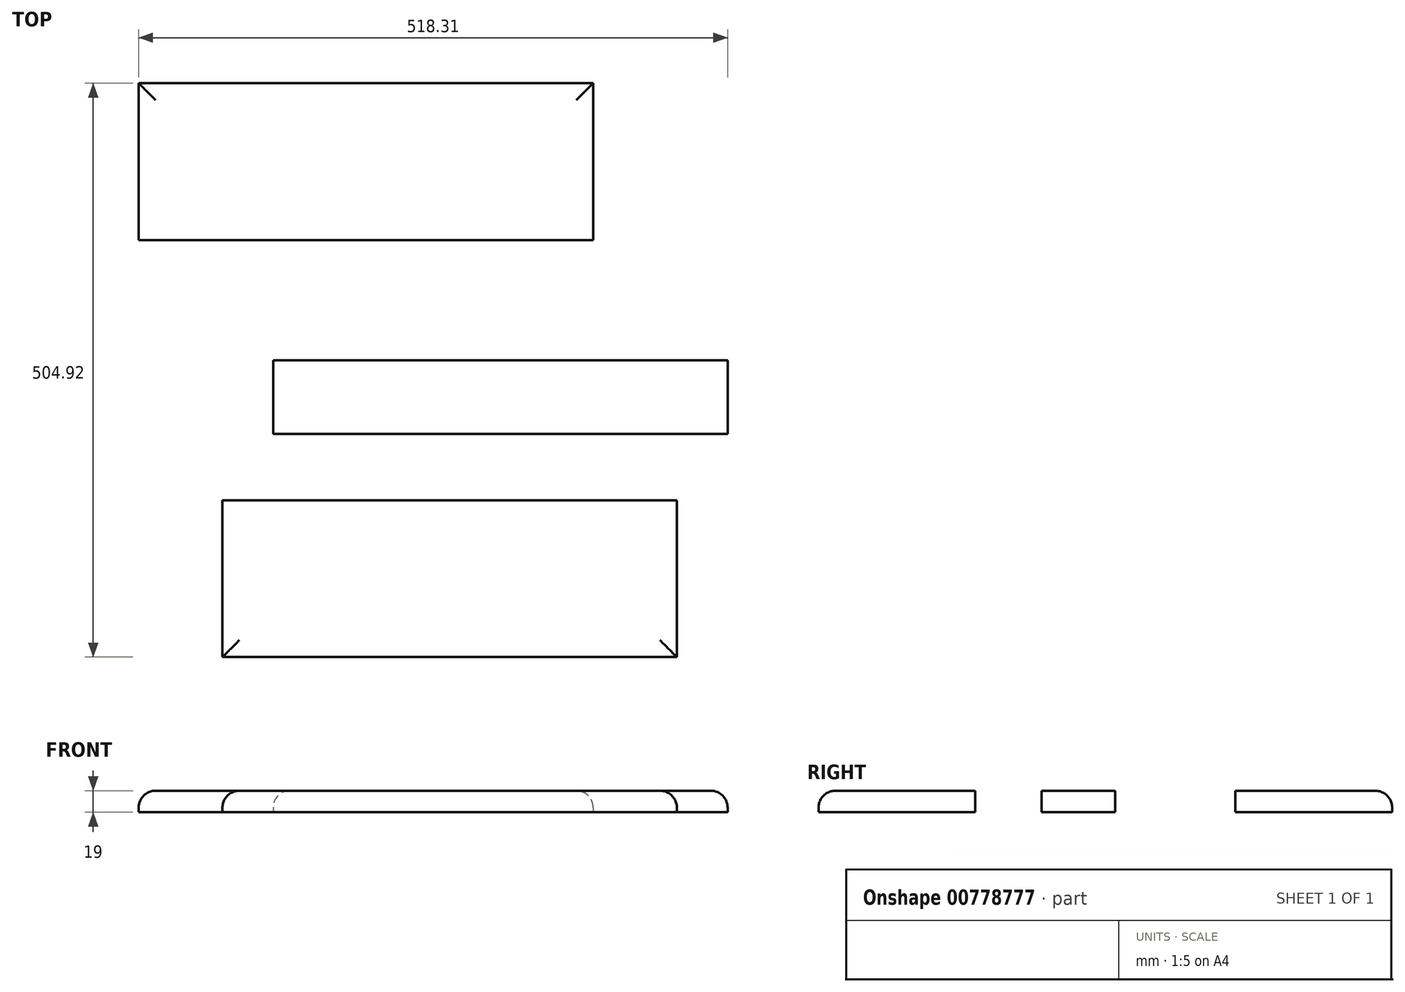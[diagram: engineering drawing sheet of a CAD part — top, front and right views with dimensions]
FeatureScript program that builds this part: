
annotation { "Feature Type Name" : "Feature", "Feature Type Description" : "" }
export const myFeature = defineFeature(function(context is Context, id is Id, definition is map)
    precondition{}
    {
        {
            var Q0;
            Q0=qCreatedBy(makeId("Top.planeOp"),FACE);
            var sketch = newSketch(context, id + "F0", { "sketchPlane" : qUnion([Q0])});
            skLineSegment(sketch, "E0.bottom", {"start": v(-199.17, 34.91) * mm, "end": v(200.83, 34.91) * mm});
            skLineSegment(sketch, "E0.top", {"start": v(-199.17, -103.09) * mm, "end": v(200.83, -103.09) * mm});
            skLineSegment(sketch, "E0.left", {"start": v(-199.17, 34.91) * mm, "end": v(-199.17, -103.09) * mm});
            skLineSegment(sketch, "E0.right", {"start": v(200.83, 34.91) * mm, "end": v(200.83, -103.09) * mm});
            skSolve(sketch);
        }
        {
            var Q0;
            Q0 = qSketchRegion(id + "F0", true);
            extrude(context, id + "F1", {"entities" : qUnion([Q0]), "depth" : 19 * mm, "offsetDistance" : 25 * mm});
        }
        {
            var Q0;
            Q0=qCreatedBy(makeId("Top.planeOp"),FACE);
            var sketch = newSketch(context, id + "F2", { "sketchPlane" : qUnion([Q0])});
            skLineSegment(sketch, "E1.bottom", {"start": v(-80.86, -208.77) * mm, "end": v(319.14, -208.77) * mm});
            skLineSegment(sketch, "E1.top", {"start": v(-80.86, -273.77) * mm, "end": v(319.14, -273.77) * mm});
            skLineSegment(sketch, "E1.left", {"start": v(-80.86, -208.77) * mm, "end": v(-80.86, -273.77) * mm});
            skLineSegment(sketch, "E1.right", {"start": v(319.14, -208.77) * mm, "end": v(319.14, -273.77) * mm});
            skSolve(sketch);
        }
        {
            var Q0;
            Q0 = qSketchRegion(id + "F2", true);
            extrude(context, id + "F3", {"entities" : qUnion([Q0]), "depth" : 19 * mm, "offsetDistance" : 25 * mm});
        }
        {
            var Q0;
            Q0=qCreatedBy(makeId("Top.planeOp"),FACE);
            var sketch = newSketch(context, id + "F4", { "sketchPlane" : qUnion([Q0])});
            skLineSegment(sketch, "E2.bottom", {"start": v(-125.48, -332) * mm, "end": v(274.52, -332) * mm});
            skLineSegment(sketch, "E2.top", {"start": v(-125.48, -470) * mm, "end": v(274.52, -470) * mm});
            skLineSegment(sketch, "E2.left", {"start": v(-125.48, -332) * mm, "end": v(-125.48, -470) * mm});
            skLineSegment(sketch, "E2.right", {"start": v(274.52, -332) * mm, "end": v(274.52, -470) * mm});
            skSolve(sketch);
        }
        {
            var Q0;
            Q0 = qSketchRegion(id + "F4", true);
            extrude(context, id + "F5", {"entities" : qUnion([Q0]), "depth" : 19 * mm, "offsetDistance" : 25 * mm});
        }
        {
            var Q0;
            Q0=makeQuery(id+"F5.opExtrude","CAP_EDGE",EDGE,{"disambiguationData":[OSD([sQuery(id+"F4.wireOp",EDGE,"E2.left")])],"isStart":false});
            var Q1;
            Q1=makeQuery(id+"F5.opExtrude","CAP_EDGE",EDGE,{"disambiguationData":[OSD([sQuery(id+"F4.wireOp",EDGE,"E2.top")])],"isStart":false});
            var Q2;
            Q2=makeQuery(id+"F5.opExtrude","CAP_EDGE",EDGE,{"disambiguationData":[OSD([sQuery(id+"F4.wireOp",EDGE,"E2.right")])],"isStart":false});
            var Q3;
            Q3=makeQuery(id+"F3.opExtrude","CAP_EDGE",EDGE,{"disambiguationData":[OSD([sQuery(id+"F2.wireOp",EDGE,"E1.right")])],"isStart":false});
            var Q4;
            Q4=makeQuery(id+"F3.opExtrude","CAP_EDGE",EDGE,{"disambiguationData":[OSD([sQuery(id+"F2.wireOp",EDGE,"E1.left")])],"isStart":false});
            var Q5;
            Q5=makeQuery(id+"F1.opExtrude","CAP_EDGE",EDGE,{"disambiguationData":[OSD([sQuery(id+"F0.wireOp",EDGE,"E0.left")])],"isStart":false});
            var Q6;
            Q6=makeQuery(id+"F1.opExtrude","CAP_EDGE",EDGE,{"disambiguationData":[OSD([sQuery(id+"F0.wireOp",EDGE,"E0.bottom")])],"isStart":false});
            var Q7;
            Q7=makeQuery(id+"F1.opExtrude","CAP_EDGE",EDGE,{"disambiguationData":[OSD([sQuery(id+"F0.wireOp",EDGE,"E0.right")])],"isStart":false});
            fillet(context, id + "F6", {"entities" : qUnion([Q0, Q1, Q2, Q3, Q4, Q5, Q6, Q7]), "radius" : 15 * mm, "tangentPropagation" : true, "allowEdgeOverflow" : false});
        }
    });
